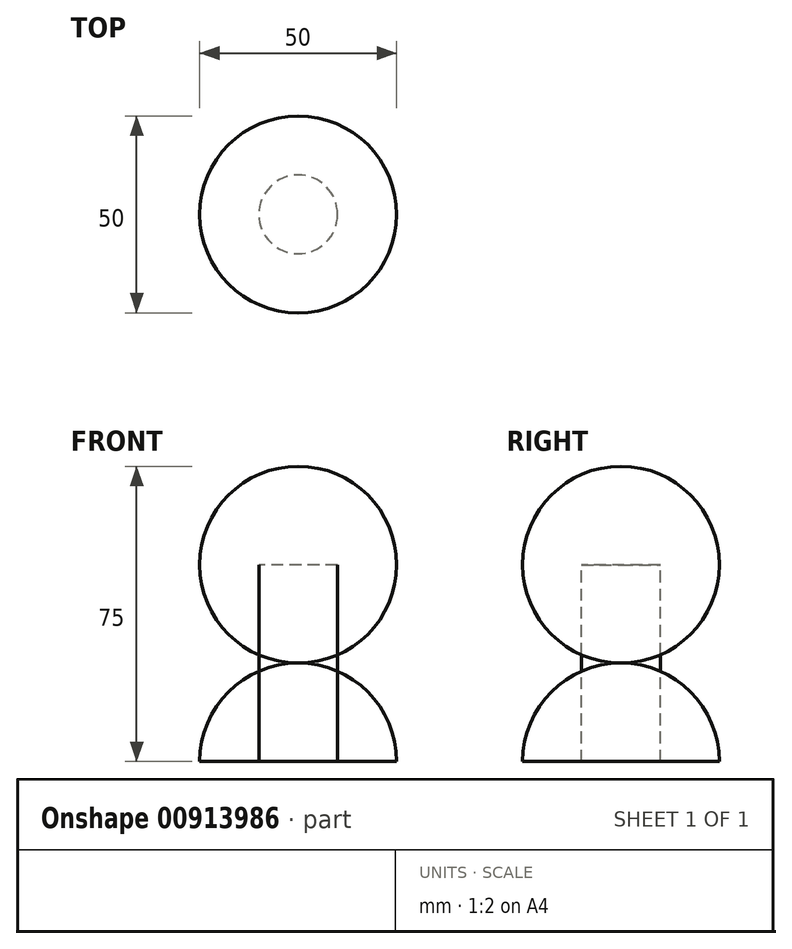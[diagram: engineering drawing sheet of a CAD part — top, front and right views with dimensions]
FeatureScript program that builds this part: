
annotation { "Feature Type Name" : "Feature", "Feature Type Description" : "" }
export const myFeature = defineFeature(function(context is Context, id is Id, definition is map)
    precondition{}
    {
        {
            var Q0;
            Q0=qCreatedBy(makeId("Top.planeOp"),FACE);
            var sketch = newSketch(context, id + "F0", { "sketchPlane" : qUnion([Q0])});
            skArc(sketch, "E0", {"start": v(25, 0) * mm, "mid": v(0, 25) * mm, "end": v(-25, 0) * mm});
            skLineSegment(sketch, "E1", {"start": v(-25, 0) * mm, "end": v(25, 0) * mm});
            skSolve(sketch);
        }
        {
            var Q0;
            Q0=makeQuery(id+"F0.imprint","IMPRINT",FACE,{"disambiguationData":[TD([[makeQuery(id+"F0.imprint","IMPRINT",EDGE,{"derivedFrom":sQuery(id+"F0.wireOp",EDGE,"E0")}),1.0]])]});
            var Q1;
            Q1=sQuery(id+"F0.wireOp",EDGE,"E1");
            revolve(context, id + "F1", {"surfaceOperationType" : NewSurfaceOperationType.NEW, "entities" : qUnion([Q0]), "axis" : qUnion([Q1]), "revolveType" : RevolveType.FULL});
        }
        {
            var Q0;
            Q0=qCreatedBy(makeId("Front.planeOp"),FACE);
            var sketch = newSketch(context, id + "F2", { "sketchPlane" : qUnion([Q0])});
            skArc(sketch, "E2", {"start": v(25, -50) * mm, "mid": v(0, -25) * mm, "end": v(-25, -50) * mm});
            skLineSegment(sketch, "E3", {"start": v(-25, -50) * mm, "end": v(25, -50) * mm});
            skSolve(sketch);
        }
        {
            var Q0;
            Q0=makeQuery(id+"F2.imprint","IMPRINT",FACE,{"disambiguationData":[TD([[makeQuery(id+"F2.imprint","IMPRINT",EDGE,{"derivedFrom":sQuery(id+"F2.wireOp",EDGE,"E2")}),1.0]])]});
            var Q1;
            Q1=sQuery(id+"F2.wireOp",EDGE,"E3");
            revolve(context, id + "F3", {"surfaceOperationType" : NewSurfaceOperationType.NEW, "entities" : qUnion([Q0]), "axis" : qUnion([Q1]), "revolveType" : RevolveType.SYMMETRIC, "angle" : 180 * degree});
        }
        {
            var Q0;
            Q0=qCreatedBy(makeId("Top.planeOp"),FACE);
            var sketch = newSketch(context, id + "F4", { "sketchPlane" : qUnion([Q0])});
            skCircle(sketch, "E4", {"center": v(0, 0) * mm, "radius": 10 * mm});
            skSolve(sketch);
        }
        {
            var Q0;
            Q0 = qSketchRegion(id + "F4", true);
            var Q1;
            Q1=sQuery(id+"F4.wireOp",EDGE,"E4");
            extrude(context, id + "F5", {"entities" : qUnion([Q0]), "surfaceEntities" : qUnion([Q1]), "oppositeDirection" : true, "depth" : 50 * mm, "offsetDistance" : 25 * mm});
        }
    });
